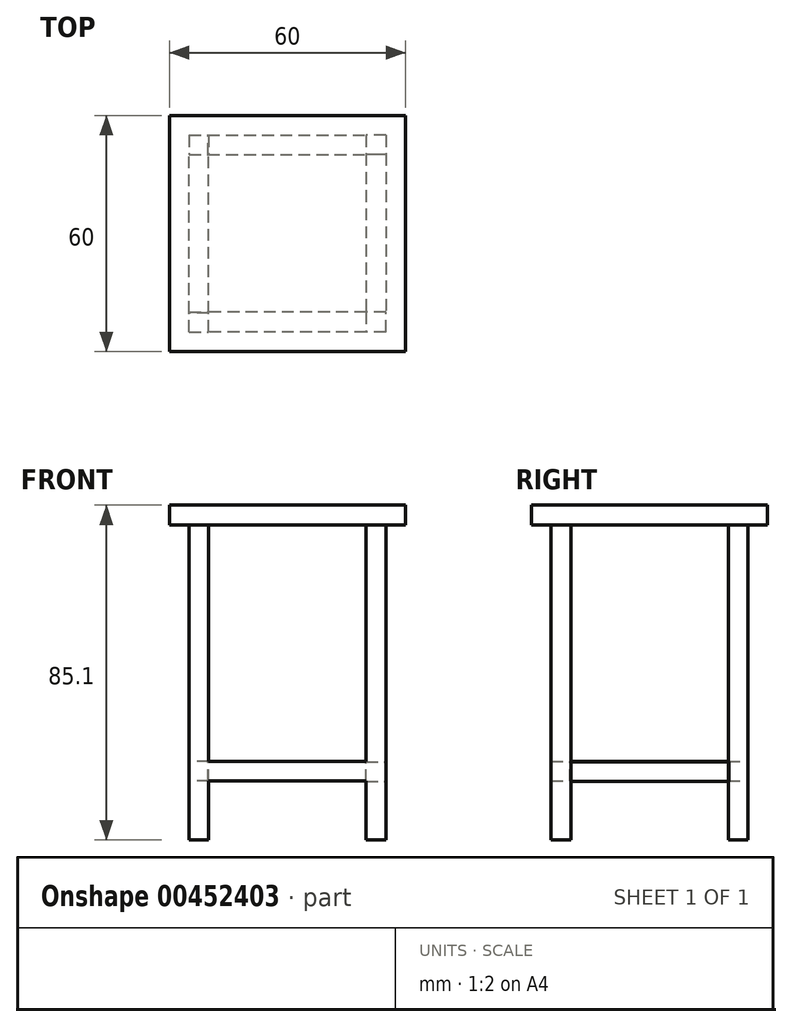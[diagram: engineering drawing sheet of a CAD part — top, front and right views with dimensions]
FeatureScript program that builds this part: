
annotation { "Feature Type Name" : "Feature", "Feature Type Description" : "" }
export const myFeature = defineFeature(function(context is Context, id is Id, definition is map)
    precondition{}
    {
        {
            var Q0;
            Q0=qCreatedBy(makeId("Top.planeOp"),FACE);
            var sketch = newSketch(context, id + "F0", { "sketchPlane" : qUnion([Q0])});
            skLineSegment(sketch, "E0.bottom", {"start": v(-30.66, 28.6) * mm, "end": v(29.34, 28.6) * mm});
            skLineSegment(sketch, "E0.top", {"start": v(-30.66, -31.4) * mm, "end": v(29.34, -31.4) * mm});
            skLineSegment(sketch, "E0.left", {"start": v(-30.66, 28.6) * mm, "end": v(-30.66, -31.4) * mm});
            skLineSegment(sketch, "E0.right", {"start": v(29.34, 28.6) * mm, "end": v(29.34, -31.4) * mm});
            skSolve(sketch);
        }
        {
            var Q0;
            Q0=makeQuery(id+"F0.imprint","IMPRINT",FACE,{"disambiguationData":[TD([[makeQuery(id+"F0.imprint","IMPRINT",EDGE,{"derivedFrom":sQuery(id+"F0.wireOp",EDGE,"E0.bottom")}),-1.0]])]});
            extrude(context, id + "F1", {"entities" : qUnion([Q0]), "depth" : 5 * mm});
        }
        {
            var Q0;
            Q0=qCreatedBy(makeId("Top.planeOp"),FACE);
            cPlane(context, id + "F2", {"entities" : qUnion([Q0]), "cplaneType" : CPlaneType.OFFSET, "offset" : 0.1 * mm, "oppositeDirection" : true, "width" : 150 * mm, "height" : 150 * mm});
        }
        {
            var Q0;
            Q0=qCreatedBy(id+"F2.planeOp",FACE);
            var sketch = newSketch(context, id + "F3", { "sketchPlane" : qUnion([Q0])});
            skPoint(sketch, "E1", {"position": v(-30.66, -31.4) * mm});
            skLineSegment(sketch, "E2", {"start": v(-30.66, -31.4) * mm, "end": v(-30.66, -26.4) * mm, "construction": true});
            skLineSegment(sketch, "E3", {"start": v(-30.66, -26.4) * mm, "end": v(-25.66, -26.4) * mm, "construction": true});
            skLineSegment(sketch, "E4.bottom", {"start": v(-25.66, -26.4) * mm, "end": v(-20.66, -26.4) * mm});
            skLineSegment(sketch, "E4.top", {"start": v(-25.66, -21.4) * mm, "end": v(-20.66, -21.4) * mm});
            skLineSegment(sketch, "E4.left", {"start": v(-25.66, -26.4) * mm, "end": v(-25.66, -21.4) * mm});
            skLineSegment(sketch, "E4.right", {"start": v(-20.66, -26.4) * mm, "end": v(-20.66, -21.4) * mm});
            skPoint(sketch, "E5", {"position": v(29.34, -31.4) * mm});
            skLineSegment(sketch, "E6", {"start": v(29.34, -31.4) * mm, "end": v(29.34, -26.4) * mm, "construction": true});
            skLineSegment(sketch, "E7", {"start": v(29.34, -26.4) * mm, "end": v(24.34, -26.4) * mm, "construction": true});
            skLineSegment(sketch, "E8.bottom", {"start": v(24.34, -26.4) * mm, "end": v(19.34, -26.4) * mm});
            skLineSegment(sketch, "E8.top", {"start": v(24.34, -21.4) * mm, "end": v(19.34, -21.4) * mm});
            skLineSegment(sketch, "E8.left", {"start": v(24.34, -26.4) * mm, "end": v(24.34, -21.4) * mm});
            skLineSegment(sketch, "E8.right", {"start": v(19.34, -26.4) * mm, "end": v(19.34, -21.4) * mm});
            skPoint(sketch, "E9", {"position": v(29.34, 28.6) * mm});
            skLineSegment(sketch, "E10", {"start": v(29.34, 28.6) * mm, "end": v(29.34, 23.6) * mm, "construction": true});
            skLineSegment(sketch, "E11", {"start": v(29.34, 23.6) * mm, "end": v(24.34, 23.6) * mm, "construction": true});
            skLineSegment(sketch, "E12.bottom", {"start": v(24.34, 23.6) * mm, "end": v(19.34, 23.6) * mm});
            skLineSegment(sketch, "E12.top", {"start": v(24.34, 18.6) * mm, "end": v(19.34, 18.6) * mm});
            skLineSegment(sketch, "E12.left", {"start": v(24.34, 23.6) * mm, "end": v(24.34, 18.6) * mm});
            skLineSegment(sketch, "E12.right", {"start": v(19.34, 23.6) * mm, "end": v(19.34, 18.6) * mm});
            skPoint(sketch, "E13", {"position": v(-30.66, 28.6) * mm});
            skLineSegment(sketch, "E14", {"start": v(-30.66, 28.6) * mm, "end": v(-30.66, 23.6) * mm, "construction": true});
            skLineSegment(sketch, "E15", {"start": v(-30.66, 23.6) * mm, "end": v(-25.66, 23.6) * mm, "construction": true});
            skLineSegment(sketch, "E16.bottom", {"start": v(-25.66, 23.6) * mm, "end": v(-20.66, 23.6) * mm});
            skLineSegment(sketch, "E16.top", {"start": v(-25.66, 18.6) * mm, "end": v(-20.66, 18.6) * mm});
            skLineSegment(sketch, "E16.left", {"start": v(-25.66, 23.6) * mm, "end": v(-25.66, 18.6) * mm});
            skLineSegment(sketch, "E16.right", {"start": v(-20.66, 23.6) * mm, "end": v(-20.66, 18.6) * mm});
            skSolve(sketch);
        }
        {
            var Q0;
            Q0=makeQuery(id+"F3.imprint","IMPRINT",FACE,{"disambiguationData":[TD([[makeQuery(id+"F3.imprint","IMPRINT",EDGE,{"derivedFrom":sQuery(id+"F3.wireOp",EDGE,"E4.bottom")}),1.0]])]});
            extrude(context, id + "F4", {"entities" : qUnion([Q0]), "oppositeDirection" : true, "depth" : 80 * mm});
        }
        {
            var Q0;
            Q0=makeQuery(id+"F3.imprint","IMPRINT",FACE,{"disambiguationData":[TD([[makeQuery(id+"F3.imprint","IMPRINT",EDGE,{"derivedFrom":sQuery(id+"F3.wireOp",EDGE,"E8.bottom")}),-1.0]])]});
            extrude(context, id + "F5", {"entities" : qUnion([Q0]), "oppositeDirection" : true, "depth" : 80 * mm});
        }
        {
            var Q0;
            Q0=makeQuery(id+"F3.imprint","IMPRINT",FACE,{"disambiguationData":[TD([[makeQuery(id+"F3.imprint","IMPRINT",EDGE,{"derivedFrom":sQuery(id+"F3.wireOp",EDGE,"E12.bottom")}),1.0]])]});
            var Q1;
            Q1=makeQuery(id+"F3.imprint","IMPRINT",FACE,{"disambiguationData":[TD([[makeQuery(id+"F3.imprint","IMPRINT",EDGE,{"derivedFrom":sQuery(id+"F3.wireOp",EDGE,"E16.bottom")}),-1.0]])]});
            extrude(context, id + "F6", {"entities" : qUnion([Q0, Q1]), "oppositeDirection" : true, "depth" : 80 * mm});
        }
        {
            var Q0;
            Q0=makeQuery(id+"F4.opExtrude","SWEPT_FACE",FACE,{"disambiguationData":[OSD([sQuery(id+"F3.wireOp",EDGE,"E4.right")])]});
            var sketch = newSketch(context, id + "F7", { "sketchPlane" : qUnion([Q0])});
            skLineSegment(sketch, "E17", {"start": v(-26.4, -80.1) * mm, "end": v(-26.4, -65.1) * mm, "construction": true});
            skLineSegment(sketch, "E18.bottom", {"start": v(-26.4, -65.1) * mm, "end": v(-21.4, -65.1) * mm});
            skLineSegment(sketch, "E18.top", {"start": v(-26.4, -60.1) * mm, "end": v(-21.4, -60.1) * mm});
            skLineSegment(sketch, "E18.left", {"start": v(-26.4, -65.1) * mm, "end": v(-26.4, -60.1) * mm});
            skLineSegment(sketch, "E18.right", {"start": v(-21.4, -65.1) * mm, "end": v(-21.4, -60.1) * mm});
            skSolve(sketch);
        }
        {
            var Q0;
            Q0 = qSketchRegion(id + "F7", true);
            extrude(context, id + "F8", {"entities" : qUnion([Q0]), "operationType" : NewBodyOperationType.ADD, "depth" : 40.1 * mm});
        }
        {
            var Q0;
            Q0=makeQuery(id+"F5.opExtrude","SWEPT_FACE",FACE,{"disambiguationData":[OSD([sQuery(id+"F3.wireOp",EDGE,"E8.top")])]});
            var sketch = newSketch(context, id + "F9", { "sketchPlane" : qUnion([Q0])});
            skLineSegment(sketch, "E19", {"start": v(-19.34, -80.1) * mm, "end": v(-19.34, -65.1) * mm, "construction": true});
            skLineSegment(sketch, "E20.bottom", {"start": v(-19.34, -60.21) * mm, "end": v(-24.34, -60.21) * mm});
            skLineSegment(sketch, "E20.top", {"start": v(-19.34, -65.21) * mm, "end": v(-24.34, -65.21) * mm});
            skLineSegment(sketch, "E20.left", {"start": v(-19.34, -60.21) * mm, "end": v(-19.34, -65.21) * mm});
            skLineSegment(sketch, "E20.right", {"start": v(-24.34, -60.21) * mm, "end": v(-24.34, -65.21) * mm});
            skSolve(sketch);
        }
        {
            var Q0;
            Q0=makeQuery(id+"F9.imprint","IMPRINT",FACE,{"disambiguationData":[TD([[makeQuery(id+"F9.imprint","IMPRINT",EDGE,{"derivedFrom":sQuery(id+"F9.wireOp",EDGE,"E20.bottom")}),1.0]])]});
            extrude(context, id + "F10", {"entities" : qUnion([Q0]), "depth" : 40.2 * mm});
        }
        {
            var Q0;
            Q0=makeQuery(id+"F6.opExtrude","SWEPT_FACE",FACE,{"disambiguationData":[OSD([sQuery(id+"F3.wireOp",EDGE,"E12.right")])]});
            var sketch = newSketch(context, id + "F11", { "sketchPlane" : qUnion([Q0])});
            skLineSegment(sketch, "E21", {"start": v(-18.6, -80.1) * mm, "end": v(-18.6, -65.1) * mm, "construction": true});
            skLineSegment(sketch, "E22.bottom", {"start": v(-18.6, -65.1) * mm, "end": v(-23.6, -65.1) * mm});
            skLineSegment(sketch, "E22.top", {"start": v(-18.6, -60.1) * mm, "end": v(-23.6, -60.1) * mm});
            skLineSegment(sketch, "E22.left", {"start": v(-18.6, -65.1) * mm, "end": v(-18.6, -60.1) * mm});
            skLineSegment(sketch, "E22.right", {"start": v(-23.6, -65.1) * mm, "end": v(-23.6, -60.1) * mm});
            skSolve(sketch);
        }
        {
            var Q0;
            Q0=makeQuery(id+"F11.imprint","IMPRINT",FACE,{"disambiguationData":[TD([[makeQuery(id+"F11.imprint","IMPRINT",EDGE,{"derivedFrom":sQuery(id+"F11.wireOp",EDGE,"E22.bottom")}),-1.0]])]});
            extrude(context, id + "F12", {"entities" : qUnion([Q0]), "depth" : 40.2 * mm});
        }
        {
            var Q0;
            Q0=makeQuery(id+"F6.opExtrude","SWEPT_FACE",FACE,{"disambiguationData":[OSD([sQuery(id+"F3.wireOp",EDGE,"E16.top")])]});
            var sketch = newSketch(context, id + "F13", { "sketchPlane" : qUnion([Q0])});
            skLineSegment(sketch, "E23", {"start": v(-20.66, -80.1) * mm, "end": v(-20.66, -65.1) * mm, "construction": true});
            skLineSegment(sketch, "E24.bottom", {"start": v(-20.66, -65.1) * mm, "end": v(-25.66, -65.1) * mm});
            skLineSegment(sketch, "E24.top", {"start": v(-20.66, -60.1) * mm, "end": v(-25.66, -60.1) * mm});
            skLineSegment(sketch, "E24.left", {"start": v(-20.66, -65.1) * mm, "end": v(-20.66, -60.1) * mm});
            skLineSegment(sketch, "E24.right", {"start": v(-25.66, -65.1) * mm, "end": v(-25.66, -60.1) * mm});
            skSolve(sketch);
        }
        {
            var Q0;
            Q0=makeQuery(id+"F13.imprint","IMPRINT",FACE,{"disambiguationData":[TD([[makeQuery(id+"F13.imprint","IMPRINT",EDGE,{"derivedFrom":sQuery(id+"F13.wireOp",EDGE,"E24.bottom")}),-1.0]])]});
            extrude(context, id + "F14", {"entities" : qUnion([Q0]), "depth" : 40.2 * mm});
        }
    });
